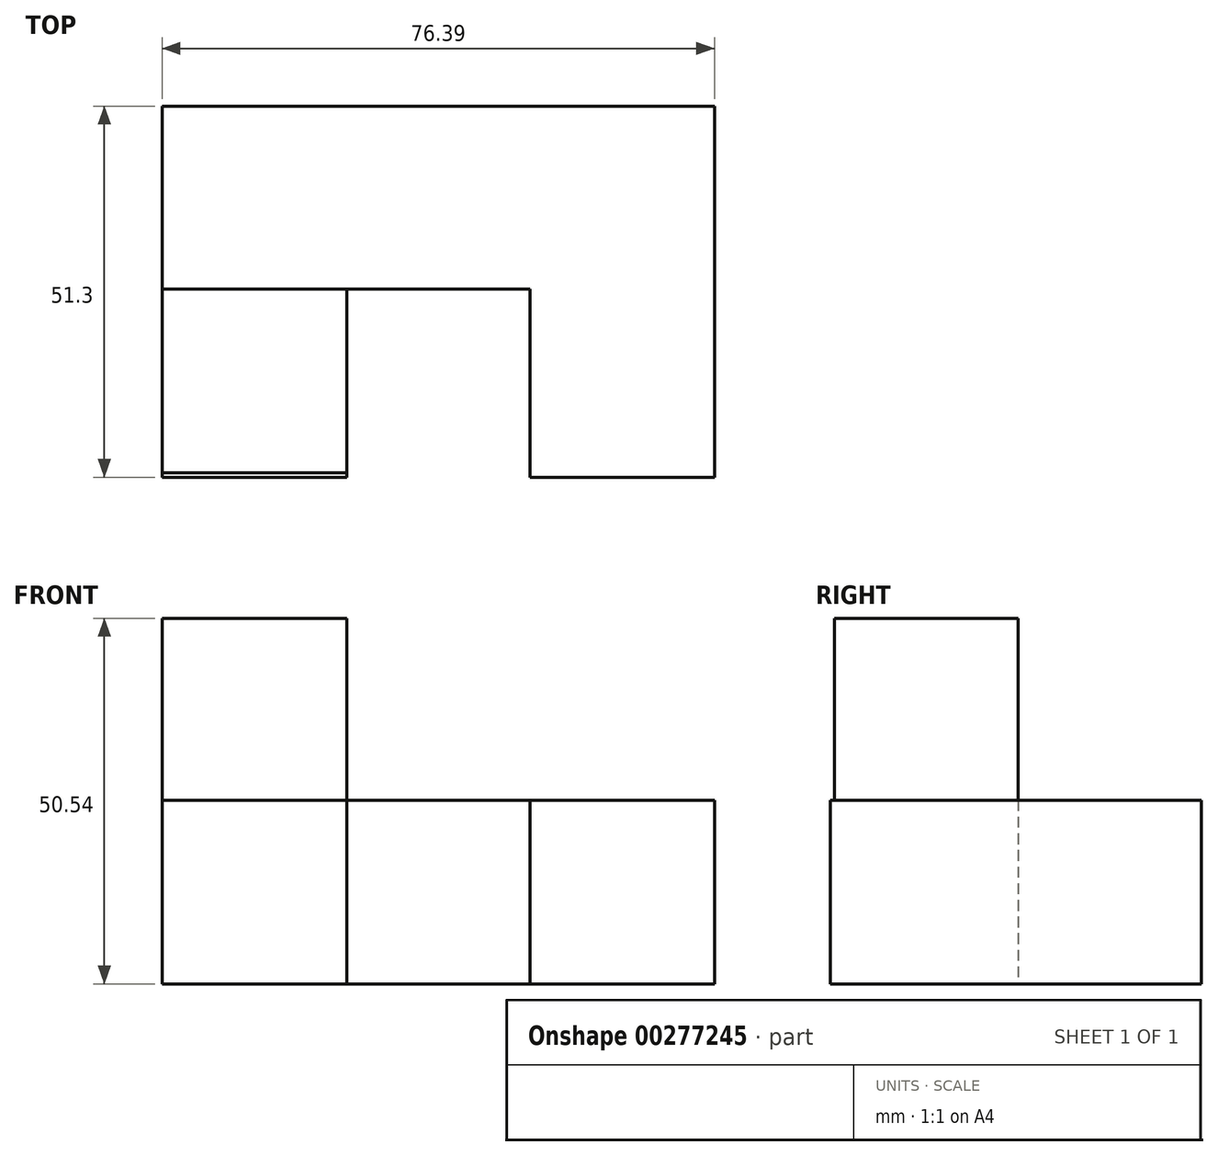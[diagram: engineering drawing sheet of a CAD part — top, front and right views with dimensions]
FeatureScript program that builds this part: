
annotation { "Feature Type Name" : "Feature", "Feature Type Description" : "" }
export const myFeature = defineFeature(function(context is Context, id is Id, definition is map)
    precondition{}
    {
        {
            var Q0;
            Q0=qCreatedBy(makeId("Top.planeOp"),FACE);
            var sketch = newSketch(context, id + "F0", { "sketchPlane" : qUnion([Q0])});
            skLineSegment(sketch, "E0", {"start": v(0, 0) * mm, "end": v(25.31, 0) * mm});
            skLineSegment(sketch, "E1", {"start": v(25.31, 0) * mm, "end": v(25.31, 25.31) * mm});
            skLineSegment(sketch, "E2", {"start": v(25.31, 25.31) * mm, "end": v(0, 25.31) * mm});
            skLineSegment(sketch, "E3", {"start": v(0, 25.31) * mm, "end": v(0, 0) * mm});
            skLineSegment(sketch, "E4", {"start": v(25.31, 25.31) * mm, "end": v(50.85, 25.31) * mm});
            skLineSegment(sketch, "E5", {"start": v(50.85, 25.31) * mm, "end": v(50.85, 0) * mm});
            skLineSegment(sketch, "E6", {"start": v(50.85, 0) * mm, "end": v(25.31, 0) * mm});
            skLineSegment(sketch, "E7", {"start": v(0, 25.31) * mm, "end": v(-25.54, 25.31) * mm});
            skLineSegment(sketch, "E8", {"start": v(-25.54, 25.31) * mm, "end": v(-25.54, 0) * mm});
            skLineSegment(sketch, "E9", {"start": v(-25.54, 0) * mm, "end": v(0, 0) * mm});
            skLineSegment(sketch, "E10", {"start": v(25.31, 0) * mm, "end": v(25.31, -26) * mm});
            skLineSegment(sketch, "E11", {"start": v(25.31, -26) * mm, "end": v(50.85, -26) * mm});
            skLineSegment(sketch, "E12", {"start": v(50.85, -26) * mm, "end": v(50.85, 0) * mm});
            skLineSegment(sketch, "E13", {"start": v(-25.54, 0) * mm, "end": v(-25.54, -26) * mm});
            skLineSegment(sketch, "E14", {"start": v(-25.54, -26) * mm, "end": v(0, -26) * mm});
            skLineSegment(sketch, "E15", {"start": v(0, -26) * mm, "end": v(0, 0) * mm});
            skSolve(sketch);
        }
        {
            var Q0;
            Q0=makeQuery(id+"F0.imprint","IMPRINT",FACE,{"disambiguationData":[TD([[makeQuery(id+"F0.imprint","IMPRINT",EDGE,{"derivedFrom":sQuery(id+"F0.wireOp",EDGE,"E0")}),1.0]])]});
            var Q1;
            Q1=makeQuery(id+"F0.imprint","IMPRINT",FACE,{"disambiguationData":[TD([[makeQuery(id+"F0.imprint","IMPRINT",EDGE,{"derivedFrom":sQuery(id+"F0.wireOp",EDGE,"E1")}),-1.0]])]});
            var Q2;
            Q2=makeQuery(id+"F0.imprint","IMPRINT",FACE,{"disambiguationData":[TD([[makeQuery(id+"F0.imprint","IMPRINT",EDGE,{"derivedFrom":sQuery(id+"F0.wireOp",EDGE,"E6")}),1.0]])]});
            var Q3;
            Q3=makeQuery(id+"F0.imprint","IMPRINT",FACE,{"disambiguationData":[TD([[makeQuery(id+"F0.imprint","IMPRINT",EDGE,{"derivedFrom":sQuery(id+"F0.wireOp",EDGE,"E9")}),-1.0]])]});
            var Q4;
            Q4=makeQuery(id+"F0.imprint","IMPRINT",FACE,{"disambiguationData":[TD([[makeQuery(id+"F0.imprint","IMPRINT",EDGE,{"derivedFrom":sQuery(id+"F0.wireOp",EDGE,"E3")}),-1.0]])]});
            extrude(context, id + "F1", {"entities" : qUnion([Q0, Q1, Q2, Q3, Q4]), "depth" : 25.4 * mm});
        }
        {
            var Q0;
            Q0=qCreatedBy(makeId("Front.planeOp"),FACE);
            var sketch = newSketch(context, id + "F2", { "sketchPlane" : qUnion([Q0])});
            skLineSegment(sketch, "E16", {"start": v(-25.5, 25.32) * mm, "end": v(-25.5, 50.54) * mm});
            skLineSegment(sketch, "E17", {"start": v(-25.5, 50.54) * mm, "end": v(0, 50.54) * mm});
            skLineSegment(sketch, "E18", {"start": v(0, 50.54) * mm, "end": v(0, 25.32) * mm});
            skLineSegment(sketch, "E19", {"start": v(0, 25.32) * mm, "end": v(-25.5, 25.32) * mm});
            skSolve(sketch);
        }
        {
            var Q0;
            Q0 = qSketchRegion(id + "F2", true);
            extrude(context, id + "F3", {"entities" : qUnion([Q0]), "operationType" : NewBodyOperationType.ADD, "depth" : 25.4 * mm});
        }
    });
